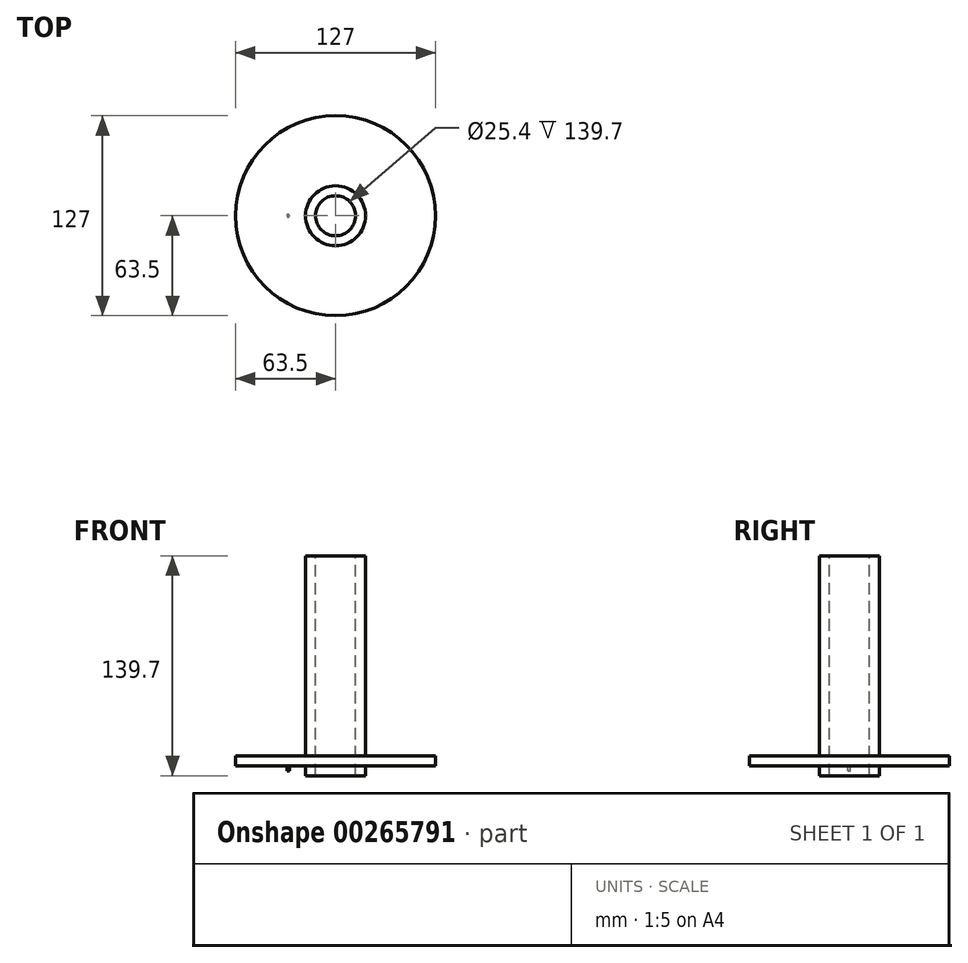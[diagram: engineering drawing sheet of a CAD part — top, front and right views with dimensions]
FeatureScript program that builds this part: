
annotation { "Feature Type Name" : "Feature", "Feature Type Description" : "" }
export const myFeature = defineFeature(function(context is Context, id is Id, definition is map)
    precondition{}
    {
        {
            var Q0;
            Q0=qCreatedBy(makeId("Top.planeOp"),FACE);
            var sketch = newSketch(context, id + "F0", { "sketchPlane" : qUnion([Q0])});
            skCircle(sketch, "E0", {"center": v(0, 0) * mm, "radius": 63.5 * mm});
            skSolve(sketch);
        }
        {
            var Q0;
            Q0=makeQuery(id+"F0.imprint","IMPRINT",FACE,{"disambiguationData":[TD([[makeQuery(id+"F0.imprint","IMPRINT",EDGE,{"derivedFrom":sQuery(id+"F0.wireOp",EDGE,"E0")}),1.0]])]});
            extrude(context, id + "F1", {"entities" : qUnion([Q0]), "depth" : 6.35 * mm});
        }
        {
            var Q0;
            Q0=makeQuery(id+"F1.opExtrude","CAP_FACE",FACE,{"disambiguationData":[OSD([sQuery(id+"F0.wireOp",EDGE,"E0")])],"isStart":true});
            var sketch = newSketch(context, id + "F2", { "sketchPlane" : qUnion([Q0])});
            skCircle(sketch, "E1", {"center": v(-30.16, 0) * mm, "radius": 0.79 * mm});
            skSolve(sketch);
        }
        {
            var Q0;
            Q0 = qSketchRegion(id + "F2", true);
            extrude(context, id + "F3", {"entities" : qUnion([Q0]), "operationType" : NewBodyOperationType.ADD, "depth" : 3.17 * mm});
        }
        {
            var Q0;
            Q0=makeQuery(id+"F1.opExtrude","CAP_FACE",FACE,{"disambiguationData":[OSD([sQuery(id+"F0.wireOp",EDGE,"E0")])],"isStart":true});
            var sketch = newSketch(context, id + "F4", { "sketchPlane" : qUnion([Q0])});
            skCircle(sketch, "E2", {"center": v(0, 0) * mm, "radius": 19.05 * mm});
            skSolve(sketch);
        }
        {
            var Q0;
            Q0 = qSketchRegion(id + "F4", true);
            extrude(context, id + "F5", {"entities" : qUnion([Q0]), "operationType" : NewBodyOperationType.ADD, "depth" : 6.35 * mm});
        }
        {
            var Q0;
            Q0=makeQuery(id+"F1.opExtrude","CAP_FACE",FACE,{"disambiguationData":[OSD([sQuery(id+"F0.wireOp",EDGE,"E0")])],"isStart":false});
            var sketch = newSketch(context, id + "F6", { "sketchPlane" : qUnion([Q0])});
            skCircle(sketch, "E3", {"center": v(0, 0) * mm, "radius": 19.05 * mm});
            skSolve(sketch);
        }
        {
            var Q0;
            Q0 = qSketchRegion(id + "F6", true);
            extrude(context, id + "F7", {"entities" : qUnion([Q0]), "operationType" : NewBodyOperationType.ADD, "depth" : 127 * mm});
        }
        {
            var Q0;
            Q0=makeQuery(id+"F7.opExtrude","CAP_FACE",FACE,{"disambiguationData":[OSD([sQuery(id+"F6.wireOp",EDGE,"E3")])],"isStart":false});
            var sketch = newSketch(context, id + "F8", { "sketchPlane" : qUnion([Q0])});
            skCircle(sketch, "E4", {"center": v(0, 0) * mm, "radius": 12.7 * mm});
            skSolve(sketch);
        }
        {
            var Q0;
            Q0 = qSketchRegion(id + "F8", true);
            extrude(context, id + "F9", {"entities" : qUnion([Q0]), "operationType" : NewBodyOperationType.REMOVE, "endBound" : BoundingType.THROUGH_ALL, "oppositeDirection" : true, "depth" : 25.4 * mm});
        }
    });
